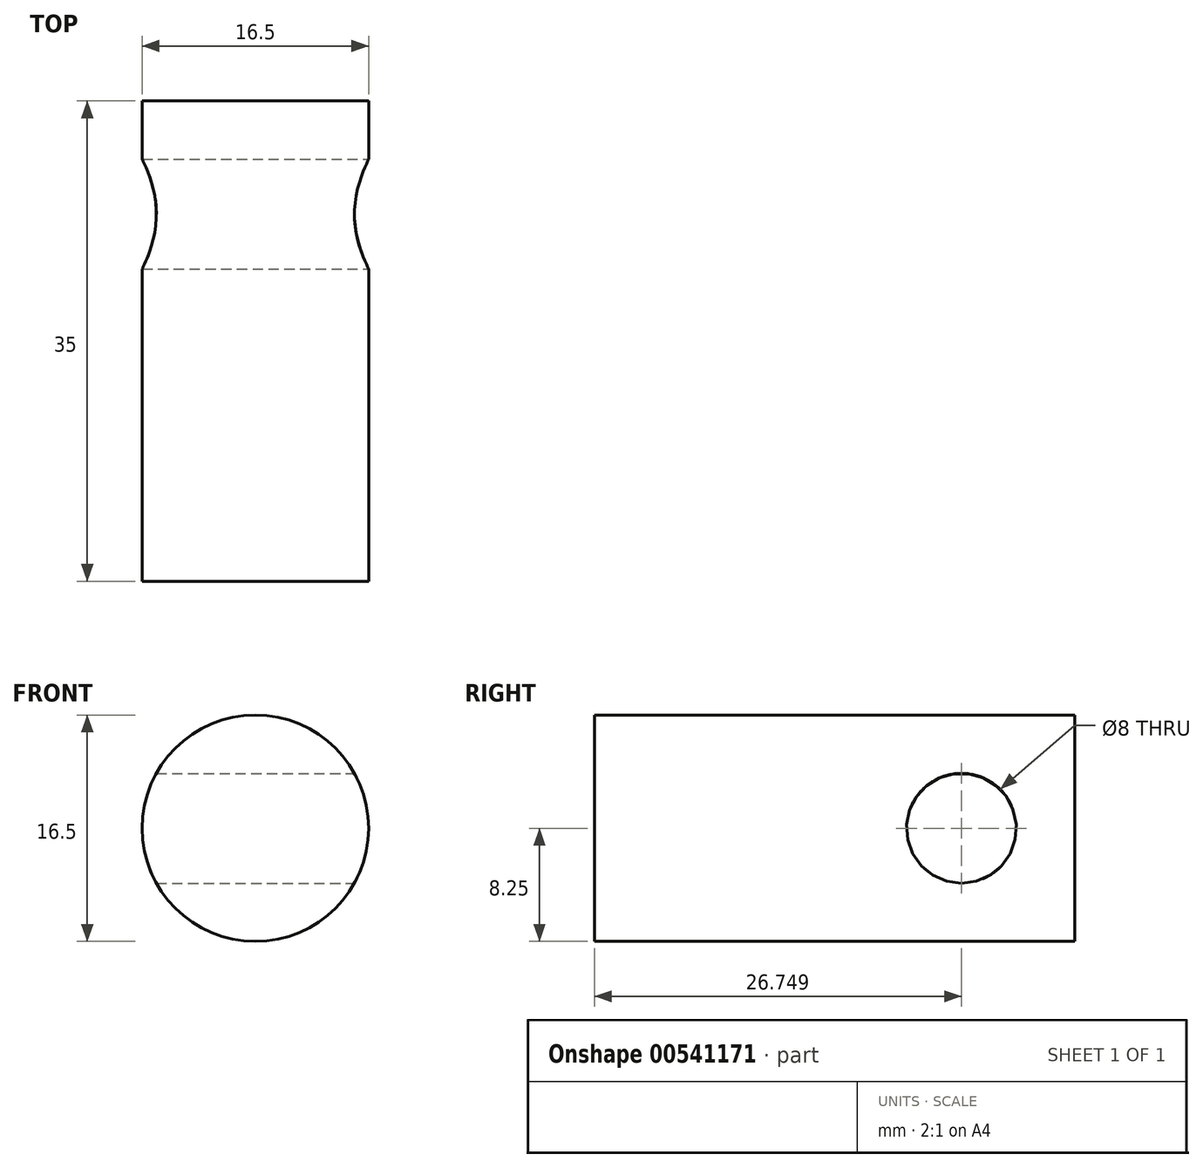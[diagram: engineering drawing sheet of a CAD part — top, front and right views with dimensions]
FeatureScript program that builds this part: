
annotation { "Feature Type Name" : "Feature", "Feature Type Description" : "" }
export const myFeature = defineFeature(function(context is Context, id is Id, definition is map)
    precondition{}
    {
        {
            var Q0;
            Q0=qCreatedBy(makeId("Front.planeOp"),FACE);
            var sketch = newSketch(context, id + "F0", { "sketchPlane" : qUnion([Q0])});
            skCircle(sketch, "E0", {"center": v(0, 0) * mm, "radius": 8.25 * mm});
            skSolve(sketch);
        }
        {
            var Q0;
            Q0=makeQuery(id+"F0.imprint","IMPRINT",FACE,{"disambiguationData":[TD([[makeQuery(id+"F0.imprint","IMPRINT",EDGE,{"derivedFrom":sQuery(id+"F0.wireOp",EDGE,"E0")}),1.0]])]});
            extrude(context, id + "F1", {"entities" : qUnion([Q0]), "depth" : 35 * mm, "offsetDistance" : 25 * mm});
        }
        {
            var Q0;
            Q0=qCreatedBy(makeId("Right.planeOp"),FACE);
            var sketch = newSketch(context, id + "F2", { "sketchPlane" : qUnion([Q0])});
            skCircle(sketch, "E1", {"center": v(-8.25, 0) * mm, "radius": 4 * mm});
            skSolve(sketch);
        }
        {
            var Q0;
            Q0=makeQuery(id+"F2.imprint","IMPRINT",FACE,{"disambiguationData":[TD([[makeQuery(id+"F2.imprint","IMPRINT",EDGE,{"derivedFrom":sQuery(id+"F2.wireOp",EDGE,"E1")}),1.0]])]});
            extrude(context, id + "F3", {"entities" : qUnion([Q0]), "operationType" : NewBodyOperationType.REMOVE, "endBound" : BoundingType.SYMMETRIC, "oppositeDirection" : true, "depth" : 38.4 * mm, "offsetDistance" : 25 * mm});
        }
    });
